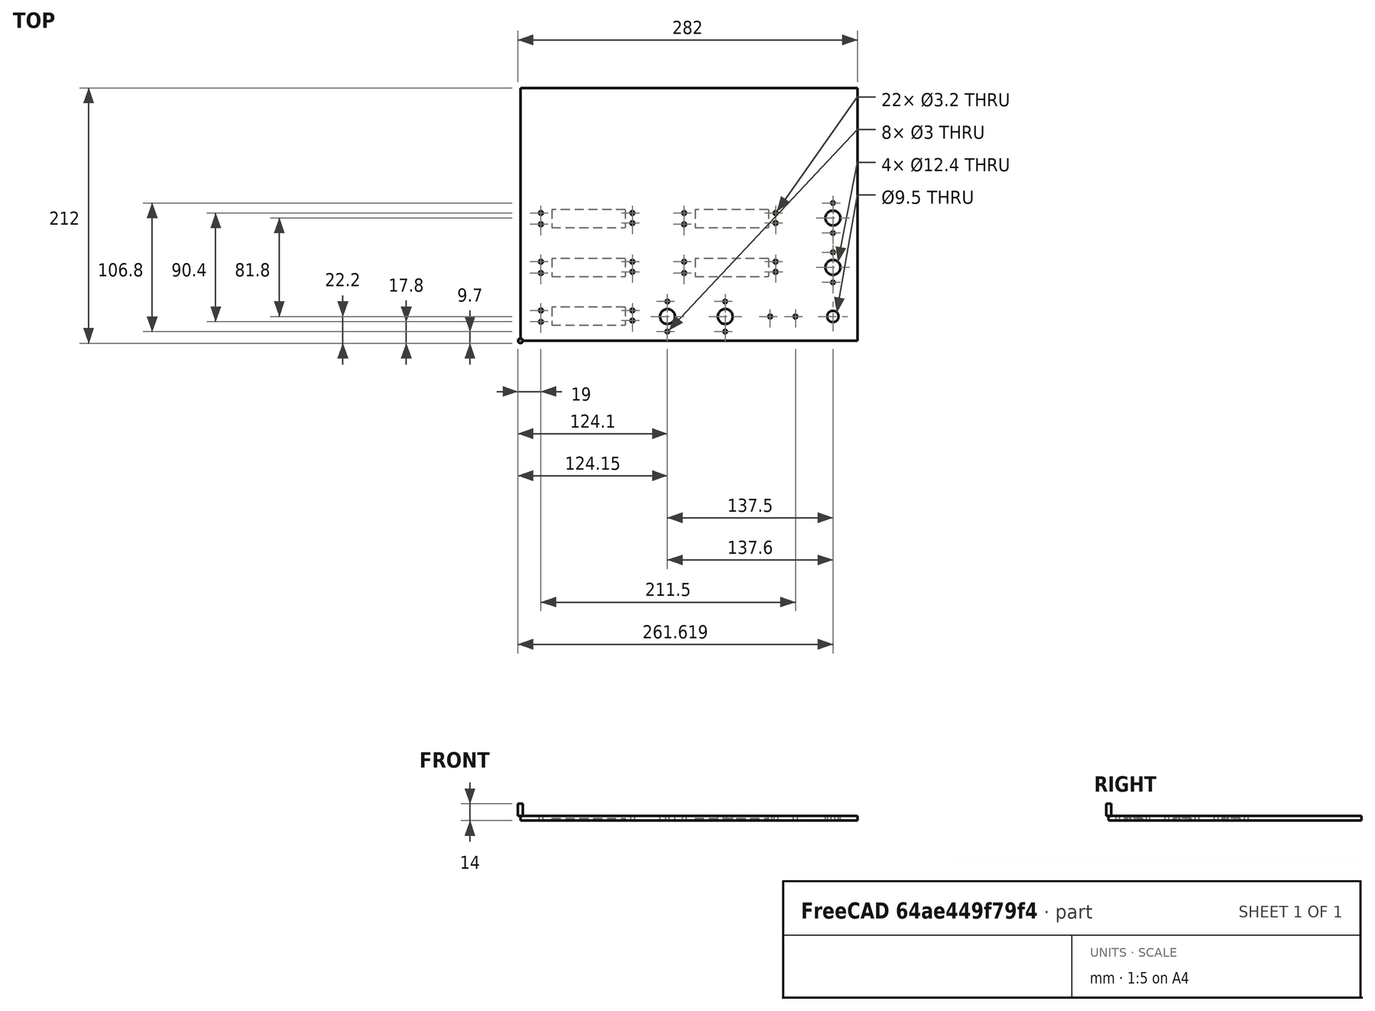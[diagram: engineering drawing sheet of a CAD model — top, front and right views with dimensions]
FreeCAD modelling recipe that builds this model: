
FCSTD DOCUMENT  (FreeCAD 0.17R13522 (Git))
Label: panel_frente_principal
License: CreativeCommons Attribution-ShareAlike
LicenseURL: http://creativecommons.org/licenses/by-sa/4.0/
objects: Part::Cut×11, Part::Feature×10, Part::Part2DObjectPython×10, Part::Box×1, Part::Cylinder×1, Part::Extrusion×1, App::DocumentObjectGroup×1
note: 34 computed .brp shape members not serialized (recipe doc carries the construction recipe); baked Part::Feature solids carry a one-line shape summary decoded from their .brp

FEATURE [Part::Box] Box  label="base principal"
  AttacherType = Attacher::AttachEngine3D
  Height = 4
  Length = 280
  Placement = pos=(0,0,-4) rot=(0,0,1;0rad)
  Width = 210
FEATURE [Part::Feature] Fusion008001001  label="perforador encoder"
  Placement = pos=(17,17,-6) rot=(1,0,0;3.14159rad)
  shape: bbox 82.5 x 15 x 10 mm, 18 faces (baked)
FEATURE [Part::Feature] Fusion008001001001  label="perforador active 1"
  Placement = pos=(17,98,-6) rot=(1,0,0;3.14159rad)
  shape: bbox 82.5 x 15 x 10 mm, 18 faces (baked)
FEATURE [Part::Feature] Fusion008001001002  label="perforador active 2"
  Placement = pos=(17,57.5,-6) rot=(1,0,0;3.14159rad)
  shape: bbox 82.5 x 15 x 10 mm, 18 faces (baked)
FEATURE [Part::Feature] Fusion008001001003  label="perforador standby 1"
  Placement = pos=(136,98,-6) rot=(1,0,0;3.14159rad)
  shape: bbox 82.5 x 15 x 10 mm, 18 faces (baked)
FEATURE [Part::Feature] Fusion008001001004  label="perforador standby 2"
  Placement = pos=(136,57.5,-6) rot=(1,0,0;3.14159rad)
  shape: bbox 82.5 x 15 x 10 mm, 18 faces (baked)
FEATURE [Part::Cut] Cut
  Base = -> Box
  Refine = true
  Tool = -> Fusion008001001
FEATURE [Part::Cut] Cut001
  Base = -> Cut
  Refine = true
  Tool = -> Fusion008001001001
FEATURE [Part::Cut] Cut002
  Base = -> Cut001
  Refine = true
  Tool = -> Fusion008001001002
FEATURE [Part::Cut] Cut003
  Base = -> Cut002
  Refine = true
  Tool = -> Fusion008001001003
FEATURE [Part::Cut] Cut004  label="base con 7 segmentos sin frente perforado"
  Base = -> Cut003
  Refine = true
  Tool = -> Fusion008001001004
FEATURE [Part::Feature] BooleanFragments001  label="perforador encoder izquierda"
  Placement = pos=(130,20.2,4) rot=(0,0,1;0rad)
  shape: bbox 45.2 x 30 x 10 mm, 34 faces, 4 solids (baked)
FEATURE [Part::Feature] BooleanFragments002  label="perforador encoder derecha"
  Placement = pos=(178,20.2,4) rot=(0,0,1;0rad)
  shape: bbox 45.2 x 30 x 10 mm, 34 faces, 4 solids (baked)
FEATURE [Part::Cut] Cut005
  Base = -> Cut004
  Refine = true
  Tool = -> BooleanFragments001
FEATURE [Part::Cut] Cut006  label="frente con agujeros displays y encoders transponder"
  Base = -> Cut005
  Refine = true
  Tool = -> BooleanFragments002
FEATURE [Part::Feature] Fusion005001  label="boton ident"
  Placement = pos=(203,14.2,1) rot=(0,0,1;0rad)
  shape: bbox 30 x 12 x 10 mm, 14 faces (baked)
FEATURE [Part::Cut] Cut007
  Base = -> Cut006
  Refine = true
  Tool = -> Fusion005001
FEATURE [Part::Part2DObjectPython] Line009  # Draft 2D object (typed FeaturePython)
  ChamferSize = 0
  Closed = false
  End = (270.847,20.2,0)
  FilletRadius = 0
  Length = 35.3471
  MakeFace = false
  Points = (2) [(235.5,20.2,0),(270.847,20.2,0)]
  Start = (235.5,20.2,0)
  Subdivisions = 0
FEATURE [Part::Cylinder] Cylinder
  Angle = 360
  AttacherType = Attacher::AttachEngine3D
  Height = 10
  Radius = 2
FEATURE [Part::Part2DObjectPython] Circle  # Draft 2D object (typed FeaturePython)
  FirstAngle = 0
  LastAngle = 0
  MakeFace = false
  Placement = pos=(269.619,20.2,4) rot=(0,0,1;0rad)
  Radius = 4.75
FEATURE [Part::Part2DObjectPython] Circle001  # Draft 2D object (typed FeaturePython)
  FirstAngle = 0
  LastAngle = 0
  MakeFace = false
  Placement = pos=(259.67,20.2,0) rot=(0,0,1;0rad)
  Radius = 14
FEATURE [Part::Extrusion] Extrude
  Base = -> Circle
  Dir = (0,0,1)
  DirMode = 2
  FaceMakerClass = Part::FaceMakerBullseye
  LengthFwd = 10
  LengthRev = 0
  Placement = pos=(-10,0,-10) rot=(0,0,1;0rad)
  Solid = true
  Symmetric = false
FEATURE [Part::Part2DObjectPython] Line014  # Draft 2D object (typed FeaturePython)
  ChamferSize = 0
  Closed = false
  End = (248.272,28.2144,0)
  FilletRadius = 0
  Length = 13.696
  MakeFace = false
  Placement = pos=(-10,0,-4) rot=(0,0,1;0rad)
  Points = (2) [(269.378,20.2,4),(258.272,28.2144,4)]
  Start = (259.378,20.2,0)
  Subdivisions = 0
FEATURE [Part::Part2DObjectPython] Line015  # Draft 2D object (typed FeaturePython)
  ChamferSize = 0
  Closed = false
  End = (254.876,33.263,0)
  FilletRadius = 0
  Length = 13.7518
  MakeFace = false
  Placement = pos=(-10,0,-4) rot=(0,0,1;0rad)
  Points = (2) [(269.174,20.2,4),(264.876,33.263,4)]
  Start = (259.174,20.2,0)
  Subdivisions = 0
FEATURE [Part::Part2DObjectPython] Line016  # Draft 2D object (typed FeaturePython)
  ChamferSize = 0
  Closed = false
  End = (263.227,33.6931,0)
  FilletRadius = 0
  Length = 14.1488
  MakeFace = false
  Placement = pos=(-10,0,-4) rot=(0,0,1;0rad)
  Points = (2) [(268.97,20.2,4),(273.227,33.6931,4)]
  Start = (258.97,20.2,0)
  Subdivisions = 0
FEATURE [Part::Part2DObjectPython] Line017  # Draft 2D object (typed FeaturePython)
  ChamferSize = 0
  Closed = false
  End = (270.612,28.9289,0)
  FilletRadius = 0
  Length = 14.5511
  MakeFace = false
  Placement = pos=(-10,0,-4) rot=(0,0,1;0rad)
  Points = (2) [(268.97,20.2,4),(280.612,28.9289,4)]
  Start = (258.97,20.2,0)
  Subdivisions = 0
FEATURE [Part::Part2DObjectPython] Line  # Draft 2D object (typed FeaturePython)
  ChamferSize = 0
  Closed = true
  End = (269.619,20.2,0)
  FilletRadius = 0
  Length = 0
  MakeFace = false
  Points = (2) [(269.619,20.2,0),(269.619,20.2,0)]
  Start = (269.619,20.2,0)
  Subdivisions = 0
FEATURE [Part::Cut] Cut008  label="base con line inferior completa"
  Base = -> Cut007
  Refine = true
  Tool = -> Extrude
FEATURE [Part::Part2DObjectPython] Line019  # Draft 2D object (typed FeaturePython)
  ChamferSize = 0
  Closed = false
  End = (259.619,169.66,0)
  FilletRadius = 0
  Length = 149.46
  MakeFace = true
  Placement = pos=(-20,0,-10) rot=(0,0,1;0rad)
  Points = (2) [(279.619,20.2,10),(279.619,169.66,10)]
  Start = (259.619,20.2,0)
  Subdivisions = 0
FEATURE [Part::Part2DObjectPython] Line023  # Draft 2D object (typed FeaturePython)
  ChamferSize = 0
  Closed = false
  End = (270.85,61,0)
  FilletRadius = 0
  Length = 96.85
  MakeFace = false
  Points = (2) [(174,61,0),(270.85,61,0)]
  Start = (174,61,0)
  Subdivisions = 0
FEATURE [App::DocumentObjectGroup] Construction
  Group = -> [Line009,Circle001,Line014,Line015,Line016,Line017,Line,Line019,Line023]
FEATURE [Part::Feature] BooleanFragments003  label="perforador para comunication 1"
  Placement = pos=(251.8,102,3) rot=(0,0,1;3.14159rad)
  shape: bbox 45.2 x 30 x 10 mm, 34 faces, 4 solids (baked)
FEATURE [Part::Feature] BooleanFragments003001  label="perforador para comunication 2"
  Placement = pos=(251.8,61,4) rot=(0,0,1;3.14159rad)
  shape: bbox 45.2 x 30 x 10 mm, 34 faces, 4 solids (baked)
FEATURE [Part::Cut] Cut009
  Base = -> Cut008
  Refine = true
  Tool = -> BooleanFragments003001
FEATURE [Part::Cut] Cut010  label="panel sin botones y sin leds"
  Base = -> Cut009
  Refine = true
  Tool = -> BooleanFragments003
